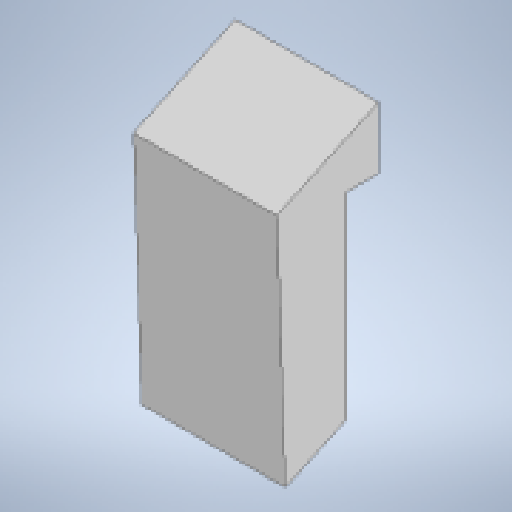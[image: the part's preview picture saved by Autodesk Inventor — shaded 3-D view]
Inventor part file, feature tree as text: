
AUTODESK INVENTOR PART (.ipt)
format: ipt  version: 2025.2 (Build 292293000, 293)  size: 163,328 bytes
history: native  units: in
note: dims shown in document units (in); Inventor stores cm internally (conversion verified against a paired STEP export)
features: sketch x4, extrude x3, reference x2, other x2
ambient origin geometry x8: Origin, YZ Plane, XZ Plane, XY Plane, X Axis, Y Axis, Z Axis, Center Point
bodies: Solid1 (feature_tree)
feature tree (11):
  extrude  "Extrusion1"  Depth=0.5in
  extrude  "Extrusion2"  Depth=1.0in TaperAngle=0.0deg
  extrude  "Extrusion3"  Depth=0.55in
  sketch  "Sketch4"  dims[d8=1.5in d9=0.0in]
  sketch  "Sketch1"  dims[d0=2.7559in d1=0.0in d2=0.5in]
  reference  "Reference1"
  reference  "Reference2"
  sketch  "Sketch2"  dims[d3=0.5in d4=1.0in d5=0.0in]
  sketch  "Sketch3"  dims[d6=0.55in d7=0.55in]
  other  "Thermal Camera Cover Assembly.iam"
  other  "1R029 Montagewinkel-Xi_7"
